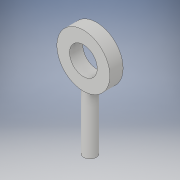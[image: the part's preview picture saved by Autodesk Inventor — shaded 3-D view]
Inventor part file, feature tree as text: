
AUTODESK INVENTOR PART (.ipt)
format: ipt  version: 2018 (Build 220112000, 112)  size: 110,080 bytes
history: native  units: in
note: dims shown in document units (in); Inventor stores cm internally (conversion verified against a paired STEP export)
features: plane x2, extrude x2, sketch x2
ambient origin geometry x8: Origin, YZ Plane, XZ Plane, XY Plane, X Axis, Y Axis, Z Axis, Center Point
bodies: Solid1 (feature_tree)
feature tree (6):
  plane  "Work Plane1"
  extrude  "Extrusion1"  Depth=0.68in
  plane  "Work Plane2"
  extrude  "Extrusion2"  Depth=0.74in
  sketch  "Sketch2"  dims[d1=0.2565in d2=0.68in]
  sketch  "Sketch3"  dims[d3=0.162in d4=0.74in d5=0.17in d6=0.0in d7=-0.339in d8=0.162in d9=0.74in d10=0.0in]
